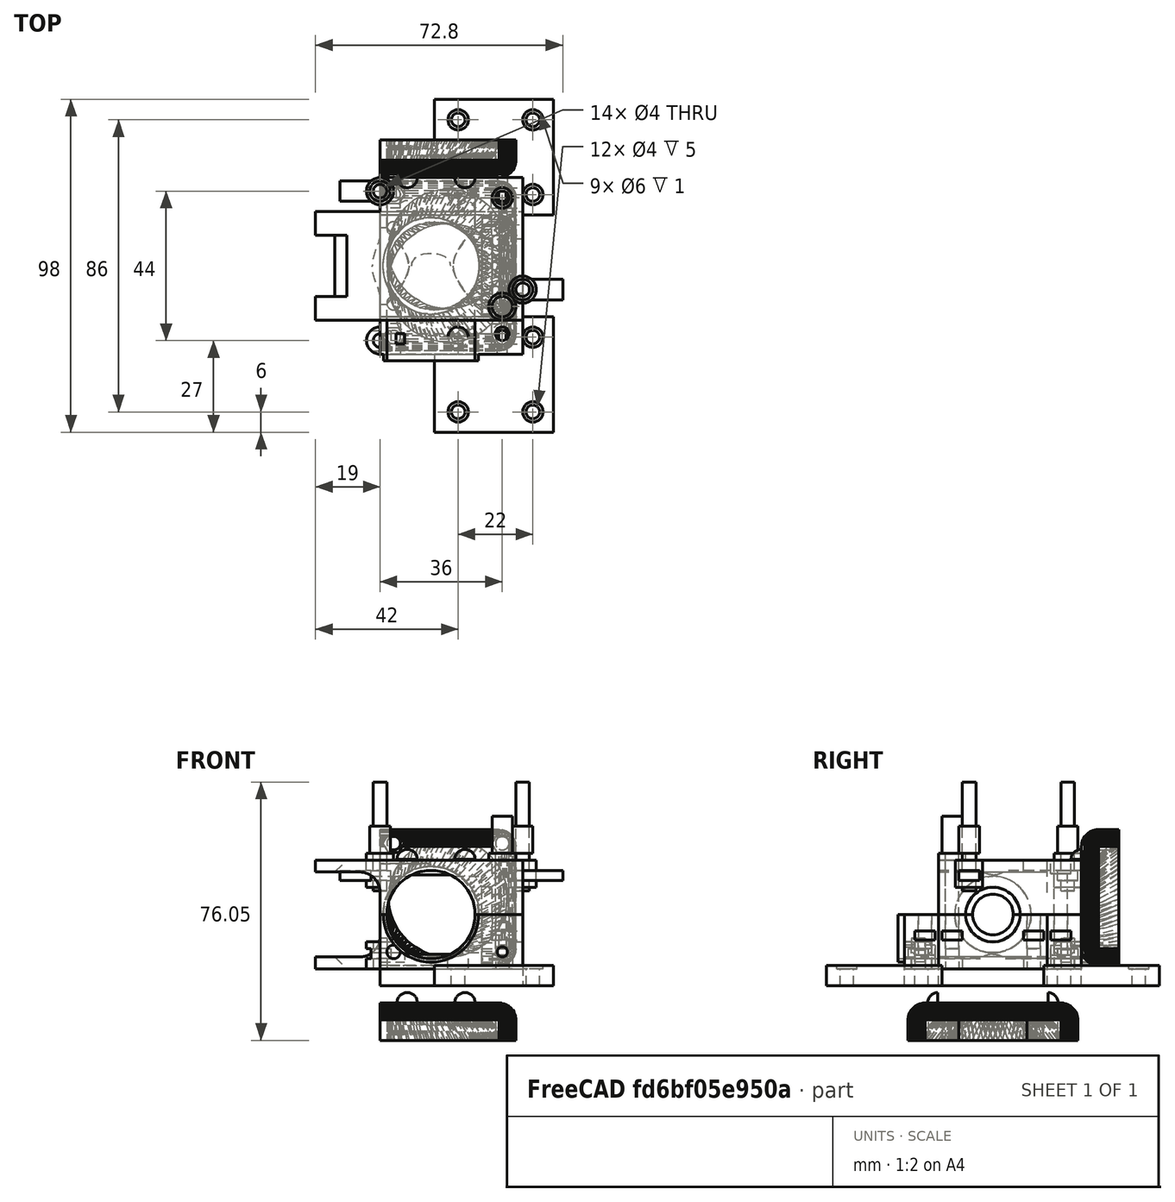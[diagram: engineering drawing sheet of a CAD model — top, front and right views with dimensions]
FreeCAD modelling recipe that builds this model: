
FCSTD DOCUMENT  (FreeCAD 0.16R6712 (Git))
Label: E3DV6_NewMount
License: All rights reserved
LicenseURL: http://en.wikipedia.org/wiki/All_rights_reserved
objects: Part::Cylinder×72, Part::MultiFuse×51, Part::Box×20, Part::Cut×12, Part::Feature×8, App::DocumentObjectGroup×7, Part::Prism×4, Part::Mirroring×3, Part::Sphere×2, Mesh::Feature×1
note: 172 computed .brp shape members not serialized (recipe doc carries the construction recipe); baked Part::Feature solids carry a one-line shape summary decoded from their .brp

FEATURE [Mesh::Feature] Left_Main_body_bltouch_40mm_fan
  Placement = pos=(-71.5,-102.7,-82) rot=(0,0,1;0rad)
FEATURE [Part::Cylinder] Cylinder
  Angle = 360
  Height = 36
  Placement = pos=(-6,0,0) rot=(0,1,0;1.5708rad)
  Radius = 11.25
FEATURE [Part::Cylinder] Cylinder001
  Angle = 360
  Height = 33
  Placement = pos=(0,0,0) rot=(0,1,0;1.5708rad)
  Radius = 8.25
FEATURE [Part::Cylinder] Cylinder002
  Angle = 360
  Height = 39
  Placement = pos=(0,0,0) rot=(0,1,0;1.5708rad)
  Radius = 6
FEATURE [Part::Cylinder] Cylinder003
  Angle = 360
  Height = 3
  Placement = pos=(39,0,0) rot=(0,1,0;1.5708rad)
  Radius = 8
FEATURE [Part::Cylinder] Cylinder004
  Angle = 360
  Height = 60
  Placement = pos=(15,38,0) rot=(1,0,0;1.5708rad)
  Radius = 13
FEATURE [Part::Cylinder] Cylinder005
  Angle = 360
  Height = 20
  Placement = pos=(5,0,17.7) rot=(0,1,0;1.5708rad)
  Radius = 6
FEATURE [Part::Cylinder] Cylinder006
  Angle = 360
  Height = 20
  Placement = pos=(5,0,-17.7) rot=(0,1,0;1.5708rad)
  Radius = 6
FEATURE [Part::MultiFuse] Fusion
  Shapes = -> [Cylinder006,Cylinder005]
FEATURE [Part::Cut] Cut
  Base = -> Cylinder004
  Tool = -> Fusion
FEATURE [Part::MultiFuse] Fusion001  label="ColdendCutAirFlow_UnterSchale"
  Shapes = -> [Cylinder,Cut,Cylinder003,Cylinder002,Cylinder001]
FEATURE [Part::Box] Box  label="CubeUnterschale"
  Height = 21
  Length = 42
  Placement = pos=(0,-16,-21) rot=(0,0,1;0rad)
  Width = 42
FEATURE [Part::Cylinder] Cylinder007
  Angle = 360
  Height = 18
  Placement = pos=(45,21,-19) rot=(0,0,1;0rad)
  Radius = 2
FEATURE [Part::Box] Box001  label="CubeOberschahle"
  Height = 16
  Length = 42
  Placement = pos=(0,-16,0) rot=(0,0,1;0rad)
  Width = 42
FEATURE [Part::Cylinder] Cylinder008
  Angle = 360
  Height = 11
  Placement = pos=(45,21,-12) rot=(0,0,1;0rad)
  Radius = 3
FEATURE [Part::MultiFuse] Fusion002
  Shapes = -> [Cylinder007,Cylinder008]
FEATURE [Part::Cylinder] Cylinder009
  Angle = 360
  Height = 18
  Placement = pos=(45,21,-19) rot=(0,0,1;0rad)
  Radius = 2
FEATURE [Part::Cylinder] Cylinder010
  Angle = 360
  Height = 11
  Placement = pos=(45,21,-12) rot=(0,0,1;0rad)
  Radius = 3
FEATURE [Part::MultiFuse] Fusion003
  Placement = pos=(-22,0,0) rot=(0,0,1;0rad)
  Shapes = -> [Cylinder009,Cylinder010]
FEATURE [Part::Cylinder] Cylinder011
  Angle = 360
  Height = 18
  Placement = pos=(45,21,-19) rot=(0,0,1;0rad)
  Radius = 2
FEATURE [Part::Cylinder] Cylinder012
  Angle = 360
  Height = 11
  Placement = pos=(45,21,-12) rot=(0,0,1;0rad)
  Radius = 3
FEATURE [Part::MultiFuse] Fusion004
  Placement = pos=(-22,22,0) rot=(0,0,1;0rad)
  Shapes = -> [Cylinder011,Cylinder012]
FEATURE [Part::Cylinder] Cylinder013
  Angle = 360
  Height = 18
  Placement = pos=(45,21,-19) rot=(0,0,1;0rad)
  Radius = 2
FEATURE [Part::Cylinder] Cylinder014
  Angle = 360
  Height = 11
  Placement = pos=(45,21,-12) rot=(0,0,1;0rad)
  Radius = 3
FEATURE [Part::MultiFuse] Fusion005
  Placement = pos=(0,22,0) rot=(0,0,1;0rad)
  Shapes = -> [Cylinder013,Cylinder014]
FEATURE [Part::Box] Box002  label="MontagePlatte"
  Height = 6
  Length = 35
  Placement = pos=(16,15,-21) rot=(0,0,1;0rad)
  Width = 34
FEATURE [Part::MultiFuse] Fusion006  label="MontageBohrungen"
  Placement = pos=(0,0,-4) rot=(0,0,1;0rad)
  Shapes = -> [Fusion002,Fusion005,Fusion004,Fusion003]
FEATURE [Part::Box] Box003  label="Cube"
  Height = 3.5
  Length = 19
  Placement = pos=(-19,-16,12.5) rot=(0,0,1;0rad)
  Width = 32
FEATURE [Part::Box] Box004  label="Cube001"
  Height = 6
  Length = 6
  Placement = pos=(-6,-16,6.5) rot=(0,0,1;0rad)
  Width = 32
FEATURE [Part::Cylinder] Cylinder015
  Angle = 360
  Height = 32
  Placement = pos=(-6,16,6.5) rot=(1,0,0;1.5708rad)
  Radius = 6
FEATURE [Part::Cut] Cut001
  Base = -> Box004
  Tool = -> Cylinder015
FEATURE [Part::MultiFuse] Fusion007
  Shapes = -> [Box003,Cut001]
FEATURE [Part::Box] Box005  label="Cube002"
  Height = 15
  Length = 15
  Placement = pos=(-30,-9,17) rot=(0,1,0;0.785398rad)
  Width = 18
FEATURE [Part::Cut] Cut002
  Base = -> Fusion007
  Tool = -> Box005
FEATURE [Part::MultiFuse] Fusion008  label="OberSchahle_0"
  Shapes = -> [Box001,Cut002]
FEATURE [Part::Cylinder] Cylinder016
  Angle = 360
  Height = 22
  Placement = pos=(45,21,-34) rot=(0,0,1;0rad)
  Radius = 2
FEATURE [Part::Cylinder] Cylinder017
  Angle = 360
  Height = 11
  Placement = pos=(45,21,-12) rot=(0,0,1;0rad)
  Radius = 3
FEATURE [Part::MultiFuse] Fusion009
  Placement = pos=(0,-4,24) rot=(0,0,1;0rad)
  Shapes = -> [Cylinder016,Cylinder017]
FEATURE [Part::Box] Box006  label="Cube003"
  Height = 2.7
  Length = 10
  Placement = pos=(41.8,14,-7.5) rot=(0,0,1;0rad)
  Width = 6
FEATURE [Part::MultiFuse] Fusion010
  Placement = pos=(-9,3,0) rot=(0,0,1;0rad)
  Shapes = -> [Fusion009,Box006]
FEATURE [Part::Cylinder] Cylinder018
  Angle = 360
  Height = 22
  Placement = pos=(45,21,-34) rot=(0,0,1;0rad)
  Radius = 2
FEATURE [Part::Cylinder] Cylinder019
  Angle = 360
  Height = 11
  Placement = pos=(45,21,-12) rot=(0,0,1;0rad)
  Radius = 3
FEATURE [Part::MultiFuse] Fusion011
  Placement = pos=(0,-4,24) rot=(0,0,1;0rad)
  Shapes = -> [Cylinder018,Cylinder019]
FEATURE [Part::Box] Box007  label="Cube004"
  Height = 2.7
  Length = 10
  Placement = pos=(41.8,14,-7.5) rot=(0,0,1;0rad)
  Width = 6
FEATURE [Part::MultiFuse] Fusion012
  Placement = pos=(-9,-29,0) rot=(0,0,1;0rad)
  Shapes = -> [Fusion011,Box007]
FEATURE [Part::MultiFuse] Fusion013  label="SchalenBohrung_UnterSchahle"
  Shapes = -> [Fusion010,Fusion012]
FEATURE [Part::Cylinder] Cylinder020
  Angle = 360
  Height = 22
  Placement = pos=(45,21,-34) rot=(0,0,1;0rad)
  Radius = 2
FEATURE [Part::Cylinder] Cylinder021
  Angle = 360
  Height = 11
  Placement = pos=(45,21,-12) rot=(0,0,1;0rad)
  Radius = 3
FEATURE [Part::MultiFuse] Fusion014
  Placement = pos=(0,-4,24) rot=(0,0,1;0rad)
  Shapes = -> [Cylinder020,Cylinder021]
FEATURE [Part::Box] Box008  label="Cube005"
  Height = 2.7
  Length = 10
  Placement = pos=(41.8,14,-7.5) rot=(0,0,1;0rad)
  Width = 6
FEATURE [Part::MultiFuse] Fusion015
  Placement = pos=(-9,3,0) rot=(0,0,1;0rad)
  Shapes = -> [Fusion014,Box008]
FEATURE [Part::Cylinder] Cylinder022
  Angle = 360
  Height = 29
  Placement = pos=(45,21,-34) rot=(0,0,1;0rad)
  Radius = 2
FEATURE [Part::Cylinder] Cylinder023
  Angle = 360
  Height = 11
  Placement = pos=(45,21,-6) rot=(0,0,1;0rad)
  Radius = 3
FEATURE [Part::MultiFuse] Fusion016
  Placement = pos=(0,-4,24) rot=(0,0,1;0rad)
  Shapes = -> [Cylinder022,Cylinder023]
FEATURE [Part::Box] Box009  label="Cube006"
  Height = 2.7
  Length = 10
  Placement = pos=(41.8,14,-7.5) rot=(0,0,1;0rad)
  Width = 6
FEATURE [Part::MultiFuse] Fusion017
  Placement = pos=(-9,-29,0) rot=(0,0,1;0rad)
  Shapes = -> [Fusion016,Box009]
FEATURE [Part::MultiFuse] Fusion018  label="SchalenBohrung_OberSchale"
  Shapes = -> [Fusion015,Fusion017]
FEATURE [Part::Cylinder] Cylinder024
  Angle = 360
  Height = 36
  Placement = pos=(-6,0,0) rot=(0,1,0;1.5708rad)
  Radius = 11.25
FEATURE [Part::Cylinder] Cylinder025
  Angle = 360
  Height = 33
  Placement = pos=(0,0,0) rot=(0,1,0;1.5708rad)
  Radius = 8.25
FEATURE [Part::Cylinder] Cylinder026
  Angle = 360
  Height = 39
  Placement = pos=(0,0,0) rot=(0,1,0;1.5708rad)
  Radius = 6
FEATURE [Part::Cylinder] Cylinder027
  Angle = 360
  Height = 3
  Placement = pos=(39,0,0) rot=(0,1,0;1.5708rad)
  Radius = 8
FEATURE [Part::Cylinder] Cylinder028
  Angle = 360
  Height = 50
  Placement = pos=(15,29,0) rot=(1,0,0;1.5708rad)
  Radius = 13
FEATURE [Part::Cylinder] Cylinder029
  Angle = 360
  Height = 20
  Placement = pos=(5,0,17.7) rot=(0,1,0;1.5708rad)
  Radius = 6
FEATURE [Part::Cylinder] Cylinder030
  Angle = 360
  Height = 20
  Placement = pos=(5,0,-17.7) rot=(0,1,0;1.5708rad)
  Radius = 6
FEATURE [Part::MultiFuse] Fusion019
  Shapes = -> [Cylinder030,Cylinder029]
FEATURE [Part::Cut] Cut003
  Base = -> Cylinder028
  Tool = -> Fusion019
FEATURE [Part::MultiFuse] Fusion020  label="ColdendCutAirFlow_OberSchale"
  Shapes = -> [Cylinder024,Cut003,Cylinder027,Cylinder026,Cylinder025]
FEATURE [Part::Box] Box010  label="Cube007"
  Height = 50
  Length = 82
  Placement = pos=(-11,-43,-84) rot=(0,0,1;0rad)
  Width = 60
FEATURE [Part::Feature] Left_Main_body_bltouch_40mm_fan001
  shape: bbox 77 x 61.5 x 45 mm, 5590 faces, 0 solids (baked)
FEATURE [Part::Box] Box011  label="Cube008"
  Height = 49
  Length = 41
  Placement = pos=(30,16,-86) rot=(0,0,1;0rad)
  Width = 16
FEATURE [Part::Box] Box012  label="Cube009"
  Height = 9
  Length = 41
  Placement = pos=(-11,16,-86) rot=(0,0,1;0rad)
  Width = 16
FEATURE [Part::MultiFuse] Fusion021
  Shapes = -> [Box010,Box012,Box011]
FEATURE [Part::Feature] Solid
  shape: bbox 77 x 61.5 x 45 mm, 4106 faces (baked)
FEATURE [Part::Cut] Cut004
  Base = -> Solid
  Placement = pos=(77,10,15) rot=(0,1,0;1.5708rad)
  Tool = -> Fusion021
FEATURE [Part::Cylinder] Cylinder031  label="FanMuffeOuter"
  Angle = 360
  Height = 2
  Placement = pos=(15,29,0) rot=(1,0,0;1.5708rad)
  Radius = 14.2
FEATURE [Part::Cylinder] Cylinder033  label="FanMuffe_UnterSchahle"
  Angle = 360
  Height = 2.2
  Placement = pos=(15,26,0) rot=(1,0,0;1.5708rad)
  Radius = 5
FEATURE [Part::Sphere] Sphere
  Angle1 = -90
  Angle2 = 90
  Angle3 = 90
  Placement = pos=(17,70,0) rot=(0,-1,0;1.5708rad)
  Radius = 3
FEATURE [Part::Sphere] Sphere001
  Angle1 = -90
  Angle2 = 90
  Angle3 = 90
  Placement = pos=(0,70,0) rot=(0,-1,0;1.5708rad)
  Radius = 3
FEATURE [Part::MultiFuse] Fusion023
  Placement = pos=(25,97,16.2) rot=(0,0,1;3.14159rad)
  Shapes = -> [Sphere,Sphere001]
FEATURE [Part::Prism] Prism
  Circumradius = 3.1
  Height = 10
  Placement = pos=(70,70,0) rot=(0,0,1;0rad)
  Polygon = 6
FEATURE [Part::Cylinder] Cylinder034
  Angle = 360
  Height = 25
  Placement = pos=(70,70,0) rot=(0,0,1;0rad)
  Radius = 2
FEATURE [Part::Cylinder] Cylinder035
  Angle = 360
  Height = 25
  Placement = pos=(70,70,0) rot=(0,0,1;0rad)
  Radius = 2
FEATURE [Part::MultiFuse] Fusion025  label="BohrungMitMutter"
  Placement = pos=(-66,19,91) rot=(-1,0,0;1.5708rad)
  Shapes = -> [Prism,Cylinder034]
FEATURE [Part::Prism] Prism001
  Circumradius = 3.1
  Height = 10
  Placement = pos=(70,70,0) rot=(0,0,1;0rad)
  Polygon = 6
FEATURE [Part::Cylinder] Cylinder036
  Angle = 360
  Height = 25
  Placement = pos=(70,70,0) rot=(0,0,1;0rad)
  Radius = 2
FEATURE [Part::MultiFuse] Fusion026  label="BohrungMitMutter001"
  Placement = pos=(-34,19,91) rot=(-1,0,0;1.5708rad)
  Shapes = -> [Prism001,Cylinder036]
FEATURE [Part::Cylinder] Cylinder037
  Angle = 360
  Height = 25
  Placement = pos=(70,70,7) rot=(0,0,1;0rad)
  Radius = 1.5
FEATURE [Part::MultiFuse] Fusion027  label="BohrungDirekt"
  Placement = pos=(-34,52,-81) rot=(1,0,0;1.5708rad)
  Shapes = -> [Cylinder035,Cylinder037]
FEATURE [Part::Cylinder] Cylinder038
  Angle = 360
  Height = 32
  Placement = pos=(70,70,0) rot=(0,0,1;0rad)
  Radius = 2
FEATURE [Part::Cylinder] Cylinder039
  Angle = 360
  Height = 25
  Placement = pos=(70,70,7) rot=(0,0,1;0rad)
  Radius = 1.5
FEATURE [Part::Box] Box013  label="Cube010"
  Height = 3
  Length = 15
  Placement = pos=(58.2,67,3) rot=(0,0,1;0rad)
  Width = 6
FEATURE [Part::MultiFuse] Fusion028
  Placement = pos=(-66,18,59) rot=(-1,0,0;1.5708rad)
  Shapes = -> [Cylinder038,Box013,Cylinder039]
FEATURE [Part::MultiFuse] Fusion029  label="BohrungFanMount01"
  Placement = pos=(0,-1,0) rot=(0,0,1;0rad)
  Shapes = -> [Fusion025,Fusion026,Fusion027,Fusion028]
FEATURE [Part::Prism] Prism002
  Circumradius = 3.1
  Height = 10
  Placement = pos=(70,70,0) rot=(0,0,1;0rad)
  Polygon = 6
FEATURE [Part::Cylinder] Cylinder040
  Angle = 360
  Height = 25
  Placement = pos=(70,70,0) rot=(0,0,1;0rad)
  Radius = 2
FEATURE [Part::Cylinder] Cylinder041
  Angle = 360
  Height = 25
  Placement = pos=(70,70,0) rot=(0,0,1;0rad)
  Radius = 2
FEATURE [Part::MultiFuse] Fusion030  label="BohrungMitMutter002"
  Placement = pos=(-66,19,91) rot=(-1,0,0;1.5708rad)
  Shapes = -> [Prism002,Cylinder040]
FEATURE [Part::Prism] Prism003
  Circumradius = 3.1
  Height = 10
  Placement = pos=(70,70,0) rot=(0,0,1;0rad)
  Polygon = 6
FEATURE [Part::Cylinder] Cylinder042
  Angle = 360
  Height = 25
  Placement = pos=(70,70,0) rot=(0,0,1;0rad)
  Radius = 2
FEATURE [Part::MultiFuse] Fusion031  label="BohrungMitMutter003"
  Placement = pos=(-34,19,91) rot=(-1,0,0;1.5708rad)
  Shapes = -> [Prism003,Cylinder042]
FEATURE [Part::Cylinder] Cylinder043
  Angle = 360
  Height = 25
  Placement = pos=(70,70,7) rot=(0,0,1;0rad)
  Radius = 1.5
FEATURE [Part::MultiFuse] Fusion032  label="BohrungDirekt001"
  Placement = pos=(-34,52,-81) rot=(1,0,0;1.5708rad)
  Shapes = -> [Cylinder041,Cylinder043]
FEATURE [Part::Cylinder] Cylinder044
  Angle = 360
  Height = 32
  Placement = pos=(70,70,0) rot=(0,0,1;0rad)
  Radius = 2
FEATURE [Part::Cylinder] Cylinder045
  Angle = 360
  Height = 25
  Placement = pos=(70,70,7) rot=(0,0,1;0rad)
  Radius = 1.5
FEATURE [Part::Box] Box014  label="Cube011"
  Height = 3
  Length = 15
  Placement = pos=(58.2,67,3) rot=(0,0,1;0rad)
  Width = 6
FEATURE [Part::MultiFuse] Fusion033
  Placement = pos=(-66,18,59) rot=(-1,0,0;1.5708rad)
  Shapes = -> [Cylinder044,Box014,Cylinder045]
FEATURE [Part::MultiFuse] Fusion034  label="BohrungFanMount_Unterschahle"
  Placement = pos=(0,-1,0) rot=(0,0,1;0rad)
  Shapes = -> [Fusion030,Fusion031,Fusion032,Fusion033]
FEATURE [Part::Cylinder] Cylinder046  label="BohrungFanMuffe_OberSchahle"
  Angle = 360
  Height = 2.2
  Placement = pos=(15,26,0) rot=(1,0,0;1.5708rad)
  Radius = 5
FEATURE [Part::MultiFuse] Fusion035  label="UnterSchahle_01"
  Shapes = -> [Box002,Box]
FEATURE [Part::MultiFuse] Fusion036  label="BohrungUnterSchale"
  Shapes = -> [Fusion001,Fusion006,Fusion013,Cylinder033,Fusion034]
FEATURE [Part::Cut] Cut007  label="UnterSchahle_03"
  Base = -> Fusion035
  Tool = -> Fusion036
FEATURE [Part::Cylinder] Cylinder047  label="Cylinder046"
  Angle = 360
  Height = 8
  Placement = pos=(0,22,8) rot=(0,0,1;0rad)
  Radius = 4
FEATURE [Part::Cylinder] Cylinder048
  Angle = 360
  Height = 32
  Placement = pos=(70,70,0) rot=(0,0,1;0rad)
  Radius = 2
FEATURE [Part::Cylinder] Cylinder049
  Angle = 360
  Height = 25
  Placement = pos=(70,70,7) rot=(0,0,1;0rad)
  Radius = 1.5
FEATURE [Part::Box] Box015  label="Cube012"
  Height = 3
  Length = 15
  Placement = pos=(58.2,67,3) rot=(0,0,1;0rad)
  Width = 6
FEATURE [Part::MultiFuse] Fusion037
  Placement = pos=(-70,-48,7) rot=(0,0,0;1.5708rad)
  Shapes = -> [Cylinder048,Box015,Cylinder049]
FEATURE [Part::Cylinder] Cylinder050  label="MountFanDuctUpper"
  Angle = 360
  Height = 8
  Placement = pos=(42,-7,8) rot=(0,0,1;0rad)
  Radius = 4
FEATURE [Part::Cylinder] Cylinder051
  Angle = 360
  Height = 32
  Placement = pos=(70,70,0) rot=(0,0,1;0rad)
  Radius = 2
FEATURE [Part::Cylinder] Cylinder052
  Angle = 360
  Height = 25
  Placement = pos=(70,70,7) rot=(0,0,1;0rad)
  Radius = 1.5
FEATURE [Part::Box] Box016  label="Cube013"
  Height = 3
  Length = 15
  Placement = pos=(58.2,67,3) rot=(0,0,1;0rad)
  Width = 6
FEATURE [Part::MultiFuse] Fusion038
  Placement = pos=(112,63,7) rot=(0,0,1;3.14159rad)
  Shapes = -> [Cylinder051,Box016,Cylinder052]
FEATURE [Part::Cylinder] Cylinder053
  Angle = 360
  Height = 8
  Placement = pos=(42,-7,18) rot=(0,0,1;0rad)
  Radius = 3
FEATURE [Part::Cylinder] Cylinder054
  Angle = 360
  Height = 8
  Placement = pos=(0,22,18) rot=(0,0,1;0rad)
  Radius = 3
FEATURE [Part::MultiFuse] Fusion039  label="FanDuctBohrung_obsolete"
  Shapes = -> [Fusion037,Cylinder054,Cylinder053,Fusion038]
FEATURE [Part::Cylinder] Cylinder055
  Angle = 360
  Height = 32
  Placement = pos=(70,70,0) rot=(0,0,1;0rad)
  Radius = 2
FEATURE [Part::Cylinder] Cylinder056
  Angle = 360
  Height = 25
  Placement = pos=(70,70,7) rot=(0,0,1;0rad)
  Radius = 1.5
FEATURE [Part::Box] Box017  label="Cube014"
  Height = 3
  Length = 15
  Placement = pos=(58.2,67,3) rot=(0,0,1;0rad)
  Width = 6
FEATURE [Part::MultiFuse] Fusion040  label="BohrungAFanDuct_OberSchale"
  Placement = pos=(-70,-48,7) rot=(0,0,1;0rad)
  Shapes = -> [Cylinder055,Box017,Cylinder056]
FEATURE [Part::Cylinder] Cylinder057
  Angle = 360
  Height = 32
  Placement = pos=(70,70,0) rot=(0,0,1;0rad)
  Radius = 2
FEATURE [Part::Cylinder] Cylinder058
  Angle = 360
  Height = 25
  Placement = pos=(70,70,7) rot=(0,0,1;0rad)
  Radius = 1.5
FEATURE [Part::Box] Box018  label="Cube015"
  Height = 3
  Length = 15
  Placement = pos=(58.2,67,3) rot=(0,0,1;0rad)
  Width = 6
FEATURE [Part::MultiFuse] Fusion041  label="BohrungFanDuctUpper001"
  Placement = pos=(112,63,7) rot=(0,0,1;3.14159rad)
  Shapes = -> [Cylinder057,Box018,Cylinder058]
FEATURE [Part::Cylinder] Cylinder059  label="BohrungFanDuctUpper"
  Angle = 360
  Height = 8
  Placement = pos=(42,-7,18) rot=(0,0,1;0rad)
  Radius = 3
FEATURE [Part::Cylinder] Cylinder060
  Angle = 360
  Height = 8
  Placement = pos=(0,22,18) rot=(0,0,1;0rad)
  Radius = 3
FEATURE [Part::Cylinder] Cylinder067
  Angle = 360
  Height = 32
  Placement = pos=(70,70,0) rot=(0,0,1;0rad)
  Radius = 2
FEATURE [Part::Cylinder] Cylinder068
  Angle = 360
  Height = 25
  Placement = pos=(70,70,7) rot=(0,0,1;0rad)
  Radius = 1.5
FEATURE [Part::Box] Box021  label="Cube018"
  Height = 3
  Length = 15
  Placement = pos=(58.2,67,3) rot=(0,0,1;0rad)
  Width = 6
FEATURE [Part::MultiFuse] Fusion048  label="BohrungFanDuct_01"
  Placement = pos=(-70,-48,7) rot=(0,0,1;0rad)
  Shapes = -> [Cylinder067,Box021,Cylinder068]
FEATURE [Part::MultiFuse] Fusion049  label="OberSchahle02"
  Shapes = -> [Cylinder047,Fusion008]
FEATURE [Part::MultiFuse] Fusion050  label="BohrungAFanDuct"
  Shapes = -> [Fusion048,Cylinder060]
FEATURE [Part::Cylinder] Cylinder069
  Angle = 360
  Height = 29
  Placement = pos=(45,21,-34) rot=(0,0,1;0rad)
  Radius = 2
FEATURE [Part::Cylinder] Cylinder070
  Angle = 360
  Height = 11
  Placement = pos=(45,21,-6) rot=(0,0,1;0rad)
  Radius = 3
FEATURE [Part::MultiFuse] Fusion051  label="BohrungBFanDuct"
  Placement = pos=(-9,-33,24) rot=(0,0,1;0rad)
  Shapes = -> [Cylinder069,Cylinder070]
FEATURE [Part::MultiFuse] Fusion052  label="BohrungOberSchale"
  Shapes = -> [Cylinder046,Fusion020,Fusion018,Fusion040]
FEATURE [Part::Cylinder] Cylinder071
  Angle = 360
  Height = 2
  Placement = pos=(0,22,20) rot=(0,0,1;0rad)
  Radius = 4
FEATURE [Part::Cylinder] Cylinder072
  Angle = 360
  Height = 2
  Placement = pos=(0,22,20) rot=(0,0,1;0rad)
  Radius = 2
FEATURE [Part::Cut] Cut008
  Base = -> Cylinder071
  Placement = pos=(0,0,-4) rot=(0,0,1;0rad)
  Tool = -> Cylinder072
FEATURE [Part::Cylinder] Cylinder073
  Angle = 360
  Height = 2
  Placement = pos=(0,22,20) rot=(0,0,1;0rad)
  Radius = 4
FEATURE [Part::Cylinder] Cylinder074
  Angle = 360
  Height = 2
  Placement = pos=(0,22,20) rot=(0,0,1;0rad)
  Radius = 2
FEATURE [Part::Cut] Cut009
  Base = -> Cylinder073
  Placement = pos=(36,-34,-4) rot=(0,0,1;0rad)
  Tool = -> Cylinder074
FEATURE [Part::MultiFuse] Fusion053  label="FanDuctMountPoints"
  Shapes = -> [Cut008,Cut009]
FEATURE [Part::Cut] Cut010  label="OberSchale_03"
  Base = -> Fusion049
  Tool = -> Fusion052
FEATURE [Part::MultiFuse] Fusion054  label="BohrungFanDuct_002"
  Shapes = -> [Fusion050,Fusion051]
FEATURE [App::DocumentObjectGroup] Group004  label="__FanDuct__"
  Group = -> [Fusion053,Fusion054]
FEATURE [App::DocumentObjectGroup] Group005  label="__COLLECTION__"
FEATURE [App::DocumentObjectGroup] Group006  label="__DRAFT__"
  Group = -> [Left_Main_body_bltouch_40mm_fan,Left_Main_body_bltouch_40mm_fan001,Fusion039,Cylinder059,Fusion041,Cylinder050]
FEATURE [Part::MultiFuse] Fusion055  label="FanMount_02"
  Placement = pos=(0,-1,0) rot=(0,0,1;0rad)
  Shapes = -> [Cut004,Fusion023]
FEATURE [Part::Cylinder] Cylinder075  label="FanMuffeOuter001"
  Angle = 180
  Height = 2
  Placement = pos=(15,29,0) rot=(1,0,0;1.5708rad)
  Radius = 14
FEATURE [Part::Cylinder] Cylinder076  label="FanMuffeInner001"
  Angle = 360
  Height = 2.2
  Placement = pos=(15,29,0) rot=(1,0,0;1.5708rad)
  Radius = 13
FEATURE [Part::Cut] Cut010005  label="FanCoupleRing_OberSchale"
  Base = -> Cylinder075
  Placement = pos=(0,-1,0) rot=(0,0,1;0rad)
  Tool = -> Cylinder076
FEATURE [Part::MultiFuse] Fusion056  label="BohrungFanMount"
  Placement = pos=(0,-1,0) rot=(0,0,1;0rad)
  Shapes = -> [Fusion029,Cylinder031]
FEATURE [Part::Cut] Cut010006  label="FanMount"
  Base = -> Fusion055
  Tool = -> Fusion056
FEATURE [App::DocumentObjectGroup] Group001  label="__FanMount__"
  Group = -> [Cut010006]
FEATURE [Part::Cylinder] Cylinder077  label="FanMuffeOuter002"
  Angle = 180
  Height = 2
  Placement = pos=(15,29,0) rot=(1,0,0;1.5708rad)
  Radius = 14
FEATURE [Part::Cylinder] Cylinder078  label="FanMuffeInner002"
  Angle = 360
  Height = 2.2
  Placement = pos=(15,29,0) rot=(1,0,0;1.5708rad)
  Radius = 13
FEATURE [Part::Cut] Cut010007  label="FanCoupleRing_UnterSchale"
  Base = -> Cylinder077
  Placement = pos=(30,-1,0) rot=(0,1,0;3.14159rad)
  Tool = -> Cylinder078
FEATURE [Part::MultiFuse] Fusion057  label="UnterSchale"
  Shapes = -> [Cut007,Cut010007]
FEATURE [App::DocumentObjectGroup] Group002  label="__UnterSchale__"
  Group = -> [Fusion057]
FEATURE [Part::MultiFuse] Fusion058  label="OberSchale"
  Shapes = -> [Cut010,Cut010005]
FEATURE [App::DocumentObjectGroup] Group003  label="__OberSchale__"
  Group = -> [Fusion058]
FEATURE [Part::Feature] Fusion058001  label="OberSchale_Left"
  Placement = pos=(0,0,0) rot=(1,0,0;3.14159rad)
  shape: bbox 61 x 44 x 16 mm, 44 faces (baked)
FEATURE [Part::Feature] Fusion057001  label="UnterSchale_Left"
  shape: bbox 51 x 65 x 21 mm, 65 faces (baked)
FEATURE [Part::Feature] Cut010006001  label="FanMount_Left"
  Placement = pos=(0,0,0) rot=(-1,0,0;1.5708rad)
  shape: bbox 40 x 40 x 14.05 mm, 638 faces, 3 solids (baked)
FEATURE [Part::Feature] Fusion058002  label="OberSchale002"
  shape: bbox 61 x 44 x 16 mm, 44 faces (baked)
FEATURE [Part::Feature] Cut010006002  label="FanMount002"
  shape: bbox 40 x 14.05 x 40 mm, 638 faces, 3 solids (baked)
FEATURE [Part::Feature] Fusion058003  label="UnterSchale002"
  shape: bbox 51 x 65 x 21 mm, 65 faces (baked)
FEATURE [Part::Mirroring] Part__Mirroring  label="FanMount_Right"
  Base = (0,0,0)
  Normal = (0,1,0)
  Placement = pos=(0,0,0) rot=(1,0,0;1.5708rad)
  Source = -> Cut010006002
FEATURE [Part::Mirroring] Part__Mirroring001  label="UnterSchale_Right"
  Base = (0,0,0)
  Normal = (0,1,0)
  Source = -> Fusion058003
FEATURE [Part::Mirroring] Part__Mirroring002  label="OberSchale_Right"
  Base = (0,0,0)
  Normal = (0,1,0)
  Placement = pos=(0,0,0) rot=(1,0,0;3.14159rad)
  Source = -> Fusion058002
FEATURE [App::DocumentObjectGroup] Group  label="Model_00"
  Group = -> [Fusion058001,Fusion057001,Cut010006001,Part__Mirroring,Part__Mirroring001,Part__Mirroring002]
